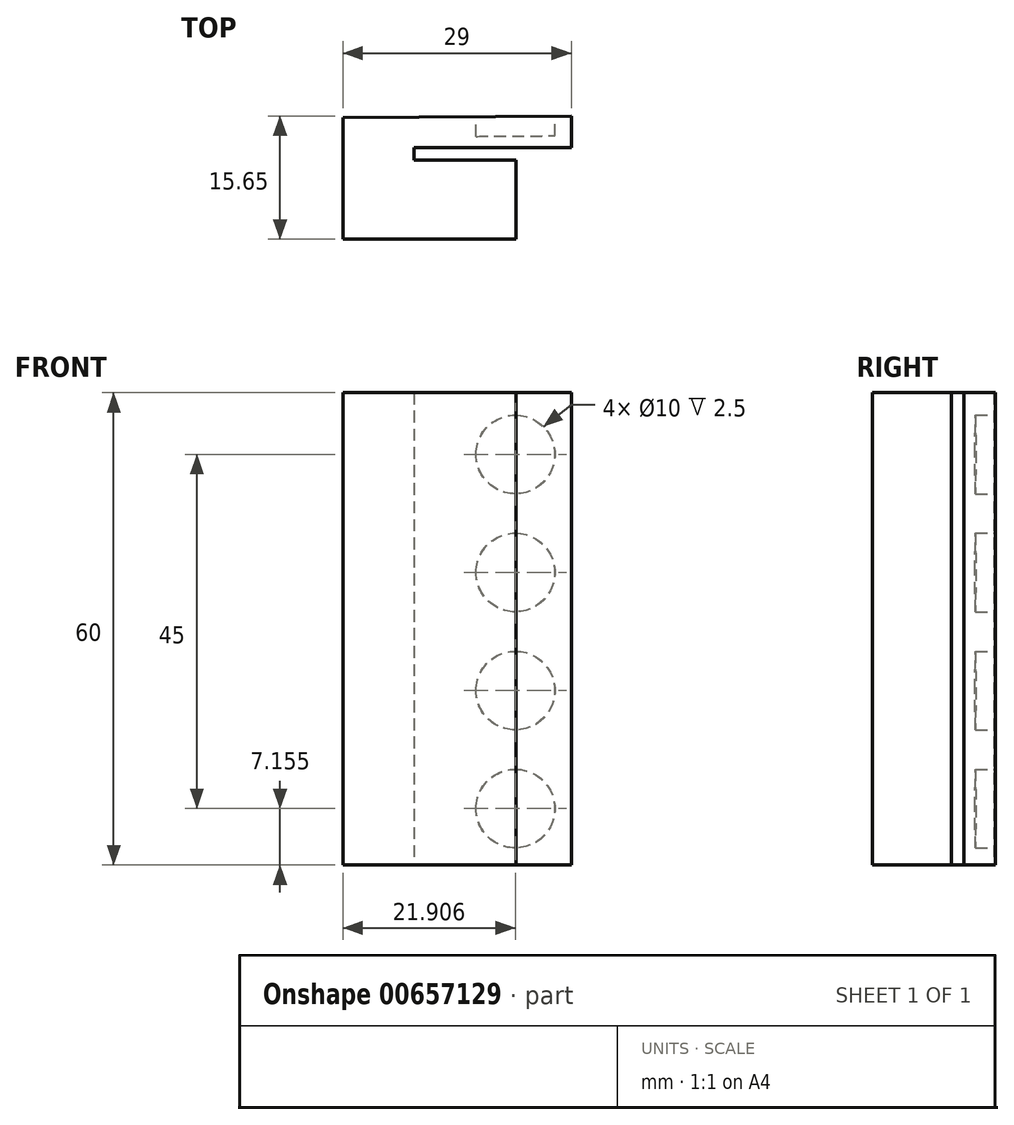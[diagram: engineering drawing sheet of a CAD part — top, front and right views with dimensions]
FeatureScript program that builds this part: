
annotation { "Feature Type Name" : "Feature", "Feature Type Description" : "" }
export const myFeature = defineFeature(function(context is Context, id is Id, definition is map)
    precondition{}
    {
        {
            var Q0;
            Q0=qCreatedBy(makeId("Top.planeOp"),FACE);
            var sketch = newSketch(context, id + "F0", { "sketchPlane" : qUnion([Q0])});
            skLineSegment(sketch, "E0", {"start": v(-37.25, 5.38) * mm, "end": v(-37.25, -10.05) * mm});
            skLineSegment(sketch, "E1", {"start": v(-37.25, -10.05) * mm, "end": v(-15.25, -10.05) * mm});
            skLineSegment(sketch, "E2", {"start": v(-15.25, -10.05) * mm, "end": v(-15.25, 0) * mm});
            skLineSegment(sketch, "E3", {"start": v(-15.25, 0) * mm, "end": v(-28.25, 0) * mm});
            skLineSegment(sketch, "E4", {"start": v(-28.25, 0) * mm, "end": v(-28.25, 1.6) * mm});
            skLineSegment(sketch, "E5", {"start": v(-28.25, 1.6) * mm, "end": v(-8.25, 1.6) * mm});
            skLineSegment(sketch, "E6", {"start": v(-8.25, 1.6) * mm, "end": v(-8.25, 5.6) * mm});
            skLineSegment(sketch, "E7", {"start": v(-8.25, 5.6) * mm, "end": v(-37.25, 5.38) * mm});
            skSolve(sketch);
        }
        {
            var Q0;
            Q0=makeQuery(id+"F0.imprint","IMPRINT",FACE,{"disambiguationData":[TD([[makeQuery(id+"F0.imprint","IMPRINT",EDGE,{"derivedFrom":sQuery(id+"F0.wireOp",EDGE,"E0")}),1.0]])]});
            extrude(context, id + "F1", {"entities" : qUnion([Q0]), "depth" : 60 * mm, "offsetDistance" : 25 * mm});
        }
        {
            var Q0;
            Q0=makeQuery(id+"F1.opExtrude","SWEPT_FACE",FACE,{"disambiguationData":[OSD([sQuery(id+"F0.wireOp",EDGE,"E7")])]});
            var sketch = newSketch(context, id + "F2", { "sketchPlane" : qUnion([Q0])});
            skCircle(sketch, "E8", {"center": v(15.31, 7.15) * mm, "radius": 5 * mm});
            skCircle(sketch, "E9.0.1.0", {"center": v(15.31, 22.15) * mm, "radius": 5 * mm});
            skCircle(sketch, "E9.0.2.0", {"center": v(15.31, 37.15) * mm, "radius": 5 * mm});
            skCircle(sketch, "E9.0.3.0", {"center": v(15.31, 52.15) * mm, "radius": 5 * mm});
            skLineSegment(sketch, "E9.direction1", {"start": v(15.31, 7.15) * mm, "end": v(35.31, 7.15) * mm, "construction": true});
            skLineSegment(sketch, "E9.direction2", {"start": v(15.31, 7.15) * mm, "end": v(15.31, 22.15) * mm, "construction": true});
            skSolve(sketch);
        }
        {
            var Q0;
            Q0=makeQuery(id+"F2.imprint","IMPRINT",FACE,{"disambiguationData":[TD([[makeQuery(id+"F2.imprint","IMPRINT",EDGE,{"derivedFrom":sQuery(id+"F2.wireOp",EDGE,"E8")}),1.0]])]});
            var Q1;
            Q1=makeQuery(id+"F2.imprint","IMPRINT",FACE,{"disambiguationData":[TD([[makeQuery(id+"F2.imprint","IMPRINT",EDGE,{"derivedFrom":sQuery(id+"F2.wireOp",EDGE,"E9.0.1.0")}),1.0]])]});
            var Q2;
            Q2=makeQuery(id+"F2.imprint","IMPRINT",FACE,{"disambiguationData":[TD([[makeQuery(id+"F2.imprint","IMPRINT",EDGE,{"derivedFrom":sQuery(id+"F2.wireOp",EDGE,"E9.0.2.0")}),1.0]])]});
            var Q3;
            Q3=makeQuery(id+"F2.imprint","IMPRINT",FACE,{"disambiguationData":[TD([[makeQuery(id+"F2.imprint","IMPRINT",EDGE,{"derivedFrom":sQuery(id+"F2.wireOp",EDGE,"E9.0.3.0")}),1.0]])]});
            extrude(context, id + "F3", {"entities" : qUnion([Q0, Q1, Q2, Q3]), "operationType" : NewBodyOperationType.REMOVE, "oppositeDirection" : true, "depth" : 2.5 * mm, "offsetDistance" : 25 * mm});
        }
    });
